# Revit family: LIXIL - 111-15 NV - COBRA STAR HEAVY PATTERN PILLAR TAP
name_source: partatom
category: Plumbing Fixtures
units: mm (PartAtom-declared; Revit-internal decimal feet)

## family parameters
Always vertical = Yes
Cut with Voids When Loaded = No
Enable Cutting in Views = No
Maintain Annotation Orientation = No
OmniClass Number = 23.45.00.00
OmniClass Title = Sanitary, Laundry, and Cleaning Equipment
Part Type = Normal
Room Calculation Point = No
Round Connector Dimension = Use Diameter
Shared = Yes
Work Plane-Based = No

## types (1)
- 111-15 NV
    Default Elevation = 0 mm  [stored 0 ft]
    Description = Cobra Star Heavy Pattern Pillar Tap to detail and spec. See sanware schedule. Available from Lixil.
    Hosted on lixil.co.za = https://www.lixil.co.za
    M _ MIXER BODY = M _ LIXIL - CHROME 01
    M _ MIXER INDICATOR 01 = M _ LIXIL - PLASTIC - BLUE 01
    M _ MIXER INDICATOR 02 = M _ LIXIL - CHROME 01
    M _ MIXER LEVER = M _ LIXIL - CHROME 01
    M _ MIXER RUBBER = M _ LIXIL - RUBBER - BLACK 01
    Product Specification = Supplier: Lixil.
Product description: Cobra Star Heavy Pattern Chrome plated pillar tap including hot & cold indices. The original star-shaped design. Well-suited for use in low water pressure environments. 1/2" BSP male connection ends. Made with de-zincification resistant brass for increased durability. Cobra TeamAssist service team on call. Includes a 20 year LIXIL Africa warranty.
20 Year Warranty Cobra LowPressure Cobra TeamAssist DZR Brass . 
Product Code: 1007850000. 
SKU Code: 111-15/NV
Barcode: 	6002194063766.
Brand: Cobra
Range: Star Heavy Pattern
Category: Taps
Sub-Category: Basins.
Colour: Chrome
Material: DZR Brass
Package Height: 60 mm
Package Width: 160 mm
Package Length: 160 mm
Package Volume: 1536 mm³
Package Weight: 530 g

Notes:
- Refer to manufacturer's and supplier's installation, maintenance and cleaning manual.
- Refer to manufacturer's and supplier's guarantees and warrantees document.

note: [stored X ft] marks values corroborated as IEEE doubles in the binary element streams (Revit-internal decimal feet)

## geometry (parser evidence)
native form markers: Sweep x12
no freeform markers — native parametric forms only
